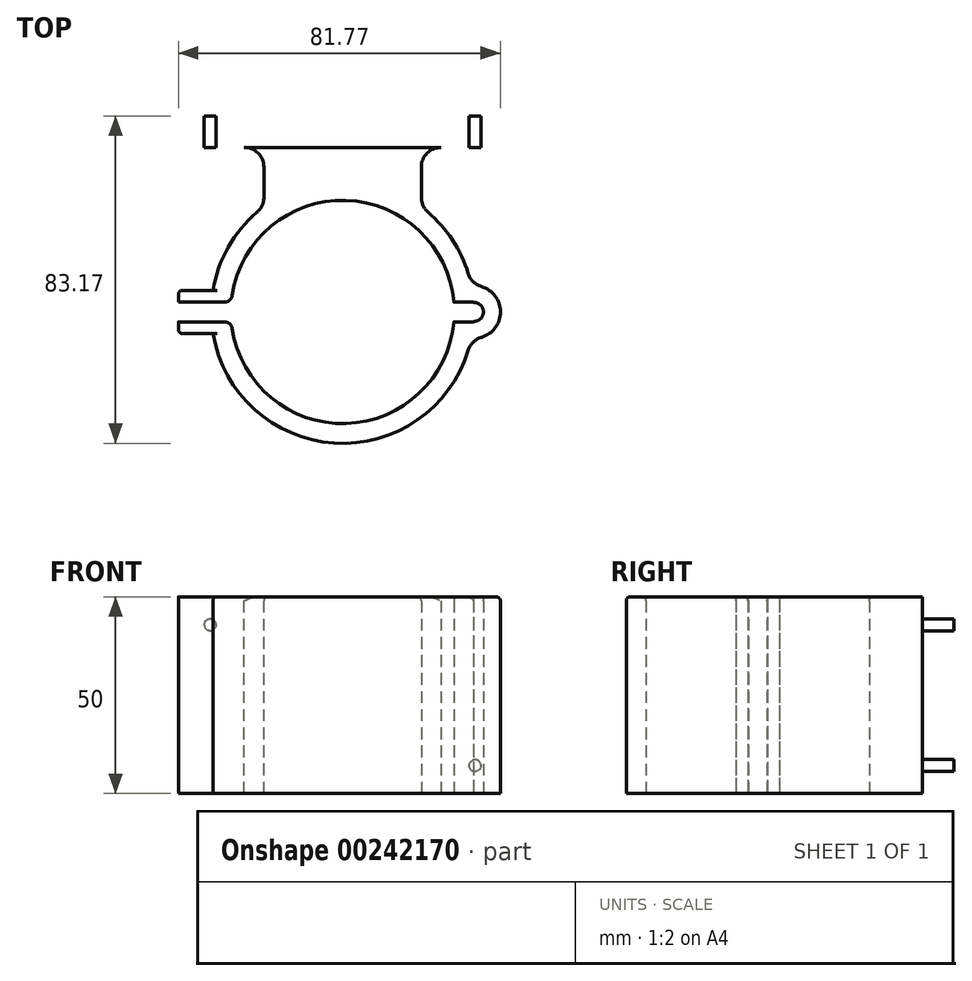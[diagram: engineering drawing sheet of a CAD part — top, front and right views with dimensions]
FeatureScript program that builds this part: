
annotation { "Feature Type Name" : "Feature", "Feature Type Description" : "" }
export const myFeature = defineFeature(function(context is Context, id is Id, definition is map)
    precondition{}
    {
        {
            var Q0;
            Q0=qCreatedBy(makeId("Top.planeOp"),FACE);
            var sketch = newSketch(context, id + "F0", { "sketchPlane" : qUnion([Q0])});
            skArc(sketch, "E0", {"start": v(-28.26, -2.5) * mm, "mid": v(0, -28.37) * mm, "end": v(28.26, -2.5) * mm});
            skArc(sketch, "E1.0", {"start": v(-32.91, -5.5) * mm, "mid": v(-0.6, -33.36) * mm, "end": v(32.7, -6.68) * mm});
            skLineSegment(sketch, "E2.top", {"start": v(40, 49.8) * mm, "end": v(-40, 49.8) * mm});
            skLineSegment(sketch, "E2.left", {"start": v(40, 41.8) * mm, "end": v(40, 49.8) * mm});
            skLineSegment(sketch, "E2.right", {"start": v(-40, 41.8) * mm, "end": v(-40, 49.8) * mm});
            skPoint(sketch, "E2.middle", {"position": v(0, 45.8) * mm});
            skPoint(sketch, "E3.middle", {"position": v(0, 33.37) * mm});
            skLineSegment(sketch, "E4", {"start": v(-20, 41.8) * mm, "end": v(-20, 26.71) * mm});
            skLineSegment(sketch, "E5", {"start": v(20, 41.8) * mm, "end": v(20, 26.71) * mm});
            skLineSegment(sketch, "E6", {"start": v(-20, 41.8) * mm, "end": v(-40, 41.8) * mm});
            skLineSegment(sketch, "E7", {"start": v(20, 41.8) * mm, "end": v(40, 41.8) * mm});
            skLineSegment(sketch, "E8", {"start": v(-33.37, 0) * mm, "end": v(33.37, 0) * mm, "construction": true});
            skLineSegment(sketch, "E9.bottom", {"start": v(-28.26, 2.5) * mm, "end": v(-33.28, 2.5) * mm});
            skLineSegment(sketch, "E9.top", {"start": v(-28.26, -2.5) * mm, "end": v(-33.28, -2.5) * mm});
            skPoint(sketch, "E9.middle", {"position": v(-33.37, 0) * mm});
            skPoint(sketch, "E10.orphan", {"position": v(-44.92, 2.5) * mm});
            skPoint(sketch, "E11.orphan", {"position": v(-31.19, -2.5) * mm});
            skPoint(sketch, "E12.orphan", {"position": v(-21.82, -2.5) * mm});
            skPoint(sketch, "E13.orphan", {"position": v(-35.55, 2.5) * mm});
            skLineSegment(sketch, "E14.bottom", {"start": v(33.28, -2.5) * mm, "end": v(28.26, -2.5) * mm});
            skLineSegment(sketch, "E14.top", {"start": v(33.28, 2.5) * mm, "end": v(28.26, 2.5) * mm});
            skPoint(sketch, "E14.middle", {"position": v(28.37, 0) * mm});
            skPoint(sketch, "E15.orphan", {"position": v(21.43, 2.5) * mm});
            skPoint(sketch, "E16.orphan", {"position": v(18, -2.5) * mm});
            skPoint(sketch, "E14.left.start.orphan", {"position": v(35.3, -2.5) * mm});
            skPoint(sketch, "E17.orphan", {"position": v(38.73, 2.5) * mm});
            skArc(sketch, "E18", {"start": v(33.28, -2.4) * mm, "mid": v(35.78, 0) * mm, "end": v(33.28, 2.4) * mm});
            skArc(sketch, "E19", {"start": v(32.7, -6.68) * mm, "mid": v(40.08, 0) * mm, "end": v(32.7, 6.68) * mm});
            skArc(sketch, "E20.trimOffspring", {"start": v(33.28, 2.4) * mm, "mid": v(33.28, 2.45) * mm, "end": v(33.28, 2.5) * mm});
            skArc(sketch, "E21.trimOffspring", {"start": v(28.26, 2.5) * mm, "mid": v(0, 28.37) * mm, "end": v(-28.26, 2.5) * mm});
            skArc(sketch, "E22.trimOffspring", {"start": v(33.28, -2.5) * mm, "mid": v(33.28, -2.45) * mm, "end": v(33.28, -2.4) * mm});
            skArc(sketch, "E23.trimOffspring", {"start": v(32.7, 6.68) * mm, "mid": v(28.19, 17.86) * mm, "end": v(20, 26.71) * mm});
            skArc(sketch, "E24.trimOffspring", {"start": v(-20, 26.71) * mm, "mid": v(-28.5, 17.35) * mm, "end": v(-32.91, 5.5) * mm});
            skLineSegment(sketch, "E25.bottom", {"start": v(-28.26, 2.5) * mm, "end": v(-41.7, 2.5) * mm});
            skLineSegment(sketch, "E25.top", {"start": v(-32.91, 5.5) * mm, "end": v(-41.7, 5.5) * mm});
            skLineSegment(sketch, "E25.right", {"start": v(-41.7, 2.5) * mm, "end": v(-41.7, 5.5) * mm});
            skLineSegment(sketch, "E26.bottom", {"start": v(-28.26, -2.5) * mm, "end": v(-41.7, -2.5) * mm});
            skLineSegment(sketch, "E26.top", {"start": v(-32.91, -5.5) * mm, "end": v(-41.7, -5.5) * mm});
            skLineSegment(sketch, "E26.right", {"start": v(-41.7, -2.5) * mm, "end": v(-41.7, -5.5) * mm});
            skSolve(sketch);
        }
        {
            var Q0;
            Q0=makeQuery(id+"F0.imprint","IMPRINT",FACE,{"disambiguationData":[TD([[makeQuery(id+"F0.imprint","IMPRINT",EDGE,{"derivedFrom":sQuery(id+"F0.wireOp",EDGE,"E0")}),-1.0]])]});
            extrude(context, id + "F1", {"entities" : qUnion([Q0]), "depth" : 50 * mm});
        }
        {
            var Q0;
            Q0=makeQuery(id+"F1.opExtrude","SWEPT_EDGE",EDGE,{"disambiguationData":[OSD([sQuery(id+"F0.wireOp",EDGE,"E1.0"),sQuery(id+"F0.wireOp",EDGE,"E19")])]});
            var Q1;
            Q1=makeQuery(id+"F1.opExtrude","SWEPT_EDGE",EDGE,{"disambiguationData":[OSD([sQuery(id+"F0.wireOp",EDGE,"E5"),sQuery(id+"F0.wireOp",EDGE,"E7")])]});
            var Q2;
            Q2=makeQuery(id+"F1.opExtrude","SWEPT_EDGE",EDGE,{"disambiguationData":[OSD([sQuery(id+"F0.wireOp",EDGE,"E5"),sQuery(id+"F0.wireOp",EDGE,"E23.trimOffspring")])]});
            var Q3;
            Q3=makeQuery(id+"F1.opExtrude","SWEPT_EDGE",EDGE,{"disambiguationData":[OSD([sQuery(id+"F0.wireOp",EDGE,"E19"),sQuery(id+"F0.wireOp",EDGE,"E23.trimOffspring")])]});
            var Q4;
            Q4=makeQuery(id+"F1.opExtrude","SWEPT_EDGE",EDGE,{"disambiguationData":[OSD([sQuery(id+"F0.wireOp",EDGE,"E4"),sQuery(id+"F0.wireOp",EDGE,"E6")])]});
            var Q5;
            Q5=makeQuery(id+"F1.opExtrude","SWEPT_EDGE",EDGE,{"disambiguationData":[OSD([sQuery(id+"F0.wireOp",EDGE,"E4"),sQuery(id+"F0.wireOp",EDGE,"E24.trimOffspring")])]});
            fillet(context, id + "F2", {"entities" : qUnion([Q0, Q1, Q2, Q3, Q4, Q5]), "radius" : 5 * mm, "tangentPropagation" : true, "allowEdgeOverflow" : false});
        }
        {
            var Q0;
            Q0=makeQuery(id+"F1.opExtrude","SWEPT_EDGE",EDGE,{"disambiguationData":[OSD([sQuery(id+"F0.wireOp",EDGE,"E9.bottom"),sQuery(id+"F0.wireOp",EDGE,"E21.trimOffspring")])]});
            var Q1;
            Q1=makeQuery(id+"F1.opExtrude","SWEPT_EDGE",EDGE,{"disambiguationData":[OSD([sQuery(id+"F0.wireOp",EDGE,"E0"),sQuery(id+"F0.wireOp",EDGE,"E9.top")])]});
            fillet(context, id + "F3", {"entities" : qUnion([Q0, Q1]), "radius" : 2 * mm, "tangentPropagation" : true, "allowEdgeOverflow" : false});
        }
        {
            var Q0;
            Q0=makeQuery(id+"F1.opExtrude","SWEPT_FACE",FACE,{"disambiguationData":[OSD([sQuery(id+"F0.wireOp",EDGE,"E2.top")])]});
            var sketch = newSketch(context, id + "F4", { "sketchPlane" : qUnion([Q0])});
            skLineSegment(sketch, "E27", {"start": v(0, 0) * mm, "end": v(0, 50) * mm, "construction": true});
            skCircle(sketch, "E28", {"center": v(-33.64, 42.87) * mm, "radius": 1.5 * mm});
            skLineSegment(sketch, "E29", {"start": v(-40, 25) * mm, "end": v(40, 25) * mm, "construction": true});
            skCircle(sketch, "E30.MirrorC", {"center": v(-33.64, 7.13) * mm, "radius": 1.5 * mm});
            skCircle(sketch, "E31.MirrorC", {"center": v(33.64, 42.87) * mm, "radius": 1.5 * mm});
            skCircle(sketch, "E32.MirrorC", {"center": v(33.64, 7.13) * mm, "radius": 1.5 * mm});
            skSolve(sketch);
        }
        {
            var Q0;
            Q0=makeQuery(id+"F4.imprint","IMPRINT",FACE,{"disambiguationData":[TD([[makeQuery(id+"F4.imprint","IMPRINT",EDGE,{"derivedFrom":sQuery(id+"F4.wireOp",EDGE,"E28")}),1.0]])]});
            var Q1;
            Q1=makeQuery(id+"F4.imprint","IMPRINT",FACE,{"disambiguationData":[TD([[makeQuery(id+"F4.imprint","IMPRINT",EDGE,{"derivedFrom":sQuery(id+"F4.wireOp",EDGE,"E30.MirrorC")}),-1.0]])]});
            var Q2;
            Q2=makeQuery(id+"F4.imprint","IMPRINT",FACE,{"disambiguationData":[TD([[makeQuery(id+"F4.imprint","IMPRINT",EDGE,{"derivedFrom":sQuery(id+"F4.wireOp",EDGE,"E32.MirrorC")}),1.0]])]});
            var Q3;
            Q3=makeQuery(id+"F4.imprint","IMPRINT",FACE,{"disambiguationData":[TD([[makeQuery(id+"F4.imprint","IMPRINT",EDGE,{"derivedFrom":sQuery(id+"F4.wireOp",EDGE,"E31.MirrorC")}),-1.0]])]});
            extrude(context, id + "F5", {"entities" : qUnion([Q0, Q1, Q2, Q3]), "operationType" : NewBodyOperationType.REMOVE, "oppositeDirection" : true, "depth" : 8 * mm});
        }
        {
            var Q0;
            Q0=makeQuery(id+"F1.opExtrude","CAP_EDGE",EDGE,{"disambiguationData":[OSD([sQuery(id+"F0.wireOp",EDGE,"E1.0")])],"isStart":false});
            var Q1;
            Q1=makeQuery(id+"F1.opExtrude","CAP_EDGE",EDGE,{"disambiguationData":[OSD([sQuery(id+"F0.wireOp",EDGE,"E24.trimOffspring")])],"isStart":false});
            var Q2;
            Q2=makeQuery(id+"F1.opExtrude","CAP_EDGE",EDGE,{"disambiguationData":[OSD([sQuery(id+"F0.wireOp",EDGE,"E21.trimOffspring")])],"isStart":false});
            var Q3;
            Q3=makeQuery(id+"F1.opExtrude","CAP_EDGE",EDGE,{"disambiguationData":[OSD([sQuery(id+"F0.wireOp",EDGE,"E0")])],"isStart":false});
            var Q4;
            Q4=makeQuery(id+"F1.opExtrude","CAP_EDGE",EDGE,{"disambiguationData":[OSD([sQuery(id+"F0.wireOp",EDGE,"E2.top")])],"isStart":false});
            var Q5;
            Q5=makeQuery(id+"F1.opExtrude","CAP_EDGE",EDGE,{"disambiguationData":[OSD([sQuery(id+"F0.wireOp",EDGE,"E2.left")])],"isStart":false});
            var Q6;
            Q6=makeQuery(id+"F1.opExtrude","CAP_EDGE",EDGE,{"disambiguationData":[OSD([sQuery(id+"F0.wireOp",EDGE,"E2.right")])],"isStart":false});
            var Q7;
            Q7=makeQuery(id+"F1.opExtrude","SWEPT_EDGE",EDGE,{"disambiguationData":[OSD([sQuery(id+"F0.wireOp",EDGE,"E26.top"),sQuery(id+"F0.wireOp",EDGE,"E26.right")])]});
            var Q8;
            Q8=makeQuery(id+"F1.opExtrude","SWEPT_EDGE",EDGE,{"disambiguationData":[OSD([sQuery(id+"F0.wireOp",EDGE,"E25.top"),sQuery(id+"F0.wireOp",EDGE,"E25.right")])]});
            fillet(context, id + "F6", {"entities" : qUnion([Q0, Q1, Q2, Q3, Q4, Q5, Q6, Q7, Q8]), "radius" : 1 * mm, "tangentPropagation" : true, "allowEdgeOverflow" : false});
        }
        {
            var Q0;
            Q0=makeQuery(id+"F1.opExtrude","CAP_EDGE",EDGE,{"disambiguationData":[OSD([sQuery(id+"F0.wireOp",EDGE,"E18")])],"isStart":false});
            fillet(context, id + "F7", {"entities" : qUnion([Q0]), "radius" : 1 * mm, "tangentPropagation" : true, "allowEdgeOverflow" : false});
        }
    });
